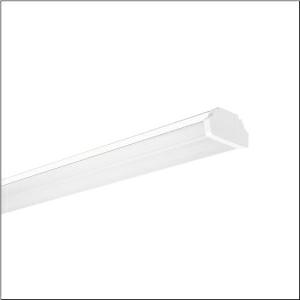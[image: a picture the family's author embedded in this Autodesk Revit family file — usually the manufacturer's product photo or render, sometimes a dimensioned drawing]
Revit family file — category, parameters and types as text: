
# Revit family: modario_31_gen_2_53bm812cv4dxd2_d5c2
name_source: partatom
category: Lighting Fixtures
units: mm (PartAtom-declared; Revit-internal decimal feet)

## family parameters
Cut with Voids When Loaded = No
Host = Face
Light Source = No
Part Type = Normal
Room Calculation Point = No
Round Connector Dimension = Use Diameter
Shared = No

## types (1)
- --- (1 x LED, 13040 lm, 68.5 W, 4000K)
    Apparent Load = 69 VA
    CIE Flux Codes = 47 80 95 93 100
    Color Rendering = 80
    Color Temperature = 4000K
    Default Elevation = 1800 mm
    Description = Modario 31 Gen.2, luminaire insert, of sheet steel, coil coated, white, length: 1.495mm, width: 81mm, height: 82mm, 5x system unit, system units: 299mm, LED rated luminous flux: 13.040lm, light colour: 840, SDCM (Standard Deviation of Colour Matching)MacAdam ≤ 3 SDCM (initial), control gear: ON/OFF Multilumen, CLOi, with plug, 3-pole, with phase selection, mains connection: 220..240V, AC, 50/60Hz, start of lifetime: 69W, end of service life: 82W, through-wiring accessed according to module size, primary optical cover: cover, of PMMA, light emission: direct distribution, primary light characteristic: symmetric, protection rating (complete): IP20, protection rating (LED compartment): IP50, insulation class (complete): insulation class I (protective earthing), certification: CE, ENEC, VDE, UKCA, impact resistance: IK03, permissible ambient temperature for indoor applications: -35..+35°C, corresponds to IFS (International Featured Standards) requirements for safety and quality in the food industry, reducing of maximum allowable ambient temperature of 5°C with ceiling mounting, IP40 when using the optional accessory 5TP9018, packaging unit: 1 piece
    Height = 92 mm
    Lamp = 1 x LED
    Lamp Light Flux = 13040 lm
    Lamp Power = 68.5 W
    Lamp count = 1
    Length = 1495 mm
    Luminous efficacy = 190 lm/W
    Manufacturer = Siteco
    ModVariant = No
    Model = 53BM812CV4DXD2
    Mounting Place = Ceiling
    Mounting Type = Pendant
    Number of Poles = 1
    OnlyDefault = Yes
    Power Factor = 1
    Product Name = Modario 31 Gen.2
    Product group = luminaire insert | ceiling pendant
    ProductGroupID = 901
    Protection Class = Protection class I
    Protection Degree = IP 20
    RLX_Detail_Level = 1
    RLX_Emergency_Light_Flux = 0 lm
    RLX_Emergency_Type = 0
    RLX_Emergency_Type_DB = No
    RlxData = <blob elided: 39989 chars, md5=eedfc022>
    Socket = socket
    Standby Power = 0 W
    System Light Flux = 13040 lm
    System Power = 69 W
    Type Comments = factory setting: luminous flux: 100 % | (A | C | E) | 161 mA
    Type Image = l_1341886.jpg
    URL = http://relux.com
    VarID = @adj_052315
    Voltage = 0 V
    Weight = 0.00 kg
    Width = 81 mm

## geometry (parser evidence)
native form markers: Blend x4, Sweep x11
no freeform markers — native parametric forms only
